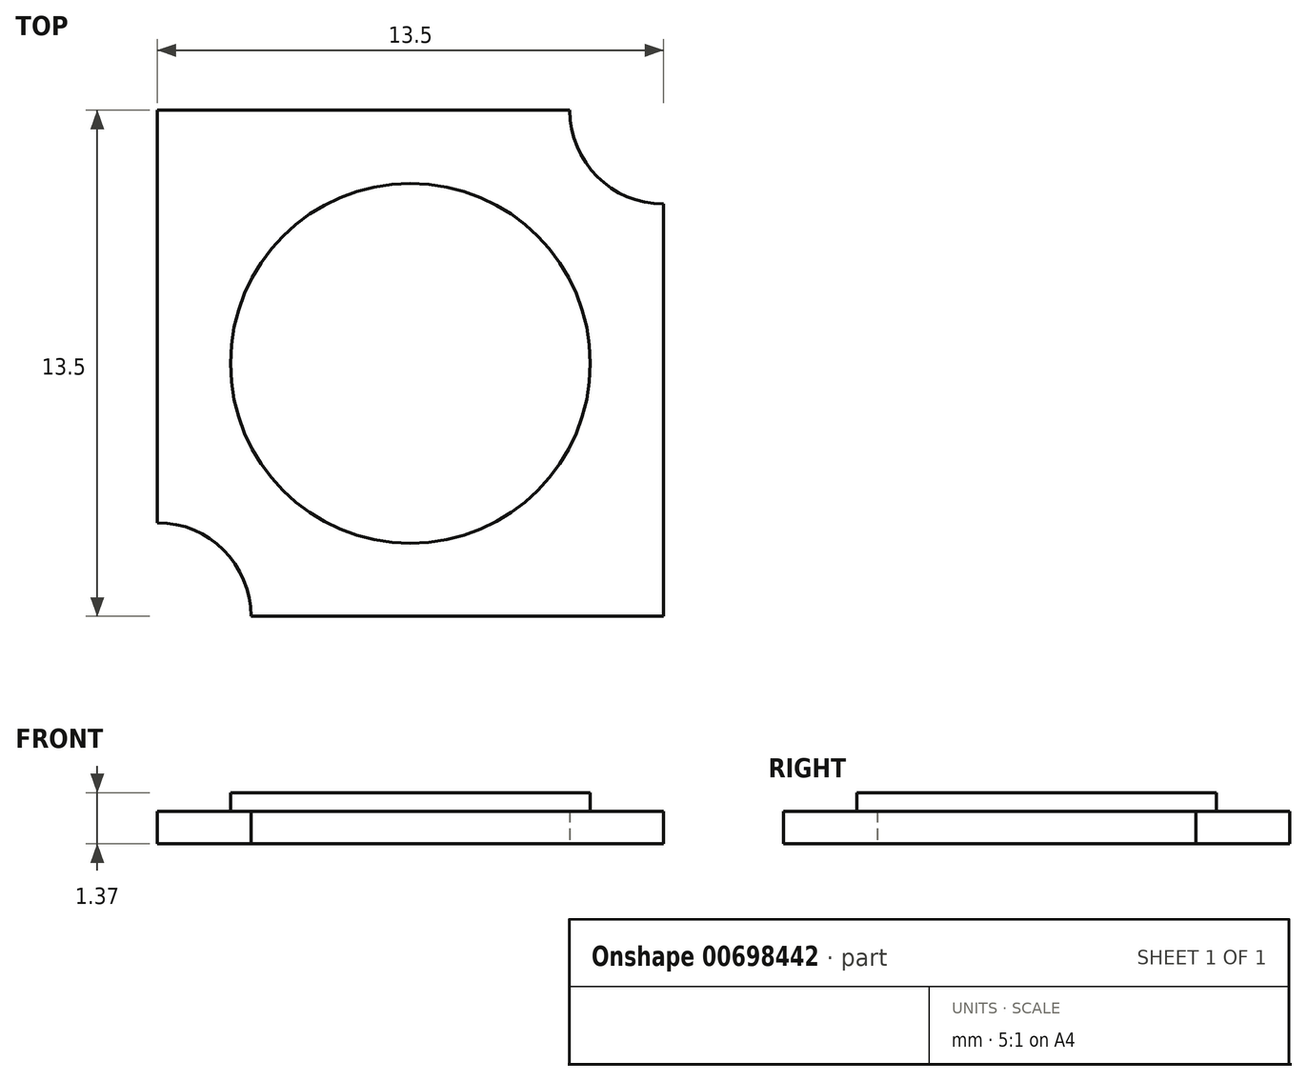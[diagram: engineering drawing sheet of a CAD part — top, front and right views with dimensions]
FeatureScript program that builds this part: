
annotation { "Feature Type Name" : "Feature", "Feature Type Description" : "" }
export const myFeature = defineFeature(function(context is Context, id is Id, definition is map)
    precondition{}
    {
        {
            var Q0;
            Q0=qCreatedBy(makeId("Top.planeOp"),FACE);
            var sketch = newSketch(context, id + "F0", { "sketchPlane" : qUnion([Q0])});
            skLineSegment(sketch, "E0.bottom", {"start": v(6.75, -6.75) * mm, "end": v(-6.75, -6.75) * mm});
            skLineSegment(sketch, "E0.top", {"start": v(6.75, 6.75) * mm, "end": v(-6.75, 6.75) * mm});
            skLineSegment(sketch, "E0.left", {"start": v(6.75, -6.75) * mm, "end": v(6.75, 6.75) * mm});
            skLineSegment(sketch, "E0.right", {"start": v(-6.75, -6.75) * mm, "end": v(-6.75, 6.75) * mm});
            skPoint(sketch, "E0.middle", {"position": v(0, 0) * mm});
            skCircle(sketch, "E1", {"center": v(6.75, 6.75) * mm, "radius": 2.5 * mm});
            skCircle(sketch, "E2", {"center": v(-6.75, -6.75) * mm, "radius": 2.5 * mm});
            skSolve(sketch);
        }
        {
            var Q0;
            {var subQ5=sQuery(id+"F0.wireOp",EDGE,"E0.left");var subQ6=sQuery(id+"F0.wireOp",EDGE,"E0.bottom");var subQ7=makeQuery(id+"F0.imprint","INTERSECT",VERTEX,{"derivedFrom":[subQ6,subQ5]});Q0=makeQuery(id+"F0.imprint","IMPRINT",FACE,{"disambiguationData":[TD([[makeQuery(id+"F0.imprint","IMPRINT",EDGE,{"disambiguationData":[TD([[subQ7,-1.0]])],"derivedFrom":subQ6}),-1.0]])]});}
            extrude(context, id + "F1", {"entities" : qUnion([Q0]), "depth" : .87 * mm, "offsetDistance" : 25 * mm});
        }
        {
            var Q0;
            Q0=makeQuery(id+"F1.opExtrude","CAP_FACE",FACE,{"disambiguationData":[OSD([sQuery(id+"F0.wireOp",EDGE,"E0.bottom"),sQuery(id+"F0.wireOp",EDGE,"E0.top"),sQuery(id+"F0.wireOp",EDGE,"E0.left"),sQuery(id+"F0.wireOp",EDGE,"E0.right"),sQuery(id+"F0.wireOp",EDGE,"E1"),sQuery(id+"F0.wireOp",EDGE,"E2")])],"isStart":false});
            var sketch = newSketch(context, id + "F2", { "sketchPlane" : qUnion([Q0])});
            skCircle(sketch, "E3", {"center": v(0, 0) * mm, "radius": 4.8 * mm});
            skSolve(sketch);
        }
        {
            var Q0;
            Q0=qSketchRegion(id+"F2",true);
            extrude(context, id + "F3", {"entities" : qUnion([Q0]), "operationType" : NewBodyOperationType.ADD, "depth" : .5 * mm, "offsetDistance" : 25 * mm});
        }
    });
